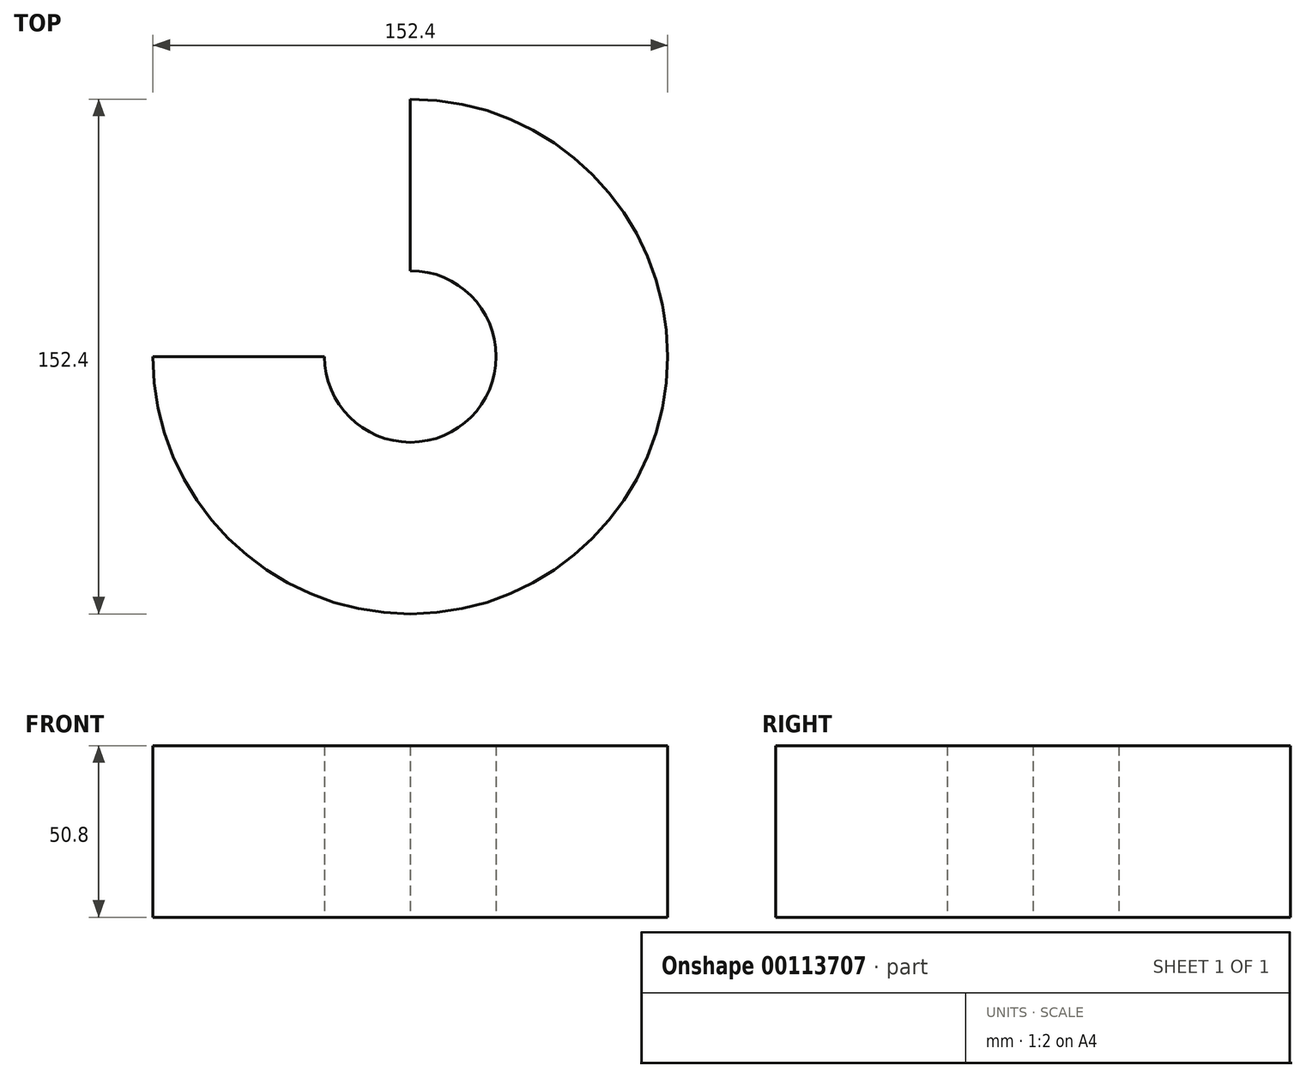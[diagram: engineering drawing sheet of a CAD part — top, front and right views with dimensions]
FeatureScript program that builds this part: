
annotation { "Feature Type Name" : "Feature", "Feature Type Description" : "" }
export const myFeature = defineFeature(function(context is Context, id is Id, definition is map)
    precondition{}
    {
        {
            var Q0;
            Q0=qCreatedBy(makeId("Top.planeOp"),FACE);
            var sketch = newSketch(context, id + "F0", { "sketchPlane" : qUnion([Q0])});
            skCircle(sketch, "E0", {"center": v(0, 0) * mm, "radius": 25.4 * mm});
            skCircle(sketch, "E1", {"center": v(0, 0) * mm, "radius": 76.2 * mm});
            skSolve(sketch);
        }
        {
            var Q0;
            Q0 = qSketchRegion(id + "F0", true);
            extrude(context, id + "F1", {"entities" : qUnion([Q0]), "depth" : 50.8 * mm});
        }
        {
            var Q0;
            Q0=makeQuery(id+"F1.opExtrude","CAP_FACE",FACE,{"disambiguationData":[OSD([sQuery(id+"F0.wireOp",EDGE,"E0"),sQuery(id+"F0.wireOp",EDGE,"E1")])],"isStart":false});
            var sketch = newSketch(context, id + "F2", { "sketchPlane" : qUnion([Q0])});
            skLineSegment(sketch, "E2.bottom", {"start": v(0, 0) * mm, "end": v(-76.2, 0) * mm});
            skLineSegment(sketch, "E2.top", {"start": v(0, 76.2) * mm, "end": v(-76.2, 76.2) * mm});
            skLineSegment(sketch, "E2.left", {"start": v(0, 0) * mm, "end": v(0, 76.2) * mm});
            skLineSegment(sketch, "E2.right", {"start": v(-76.2, 0) * mm, "end": v(-76.2, 76.2) * mm});
            skSolve(sketch);
        }
        {
            var Q0;
            Q0 = qSketchRegion(id + "F2", true);
            extrude(context, id + "F3", {"entities" : qUnion([Q0]), "operationType" : NewBodyOperationType.REMOVE, "endBound" : BoundingType.THROUGH_ALL, "oppositeDirection" : true, "depth" : 25.4 * mm});
        }
    });
